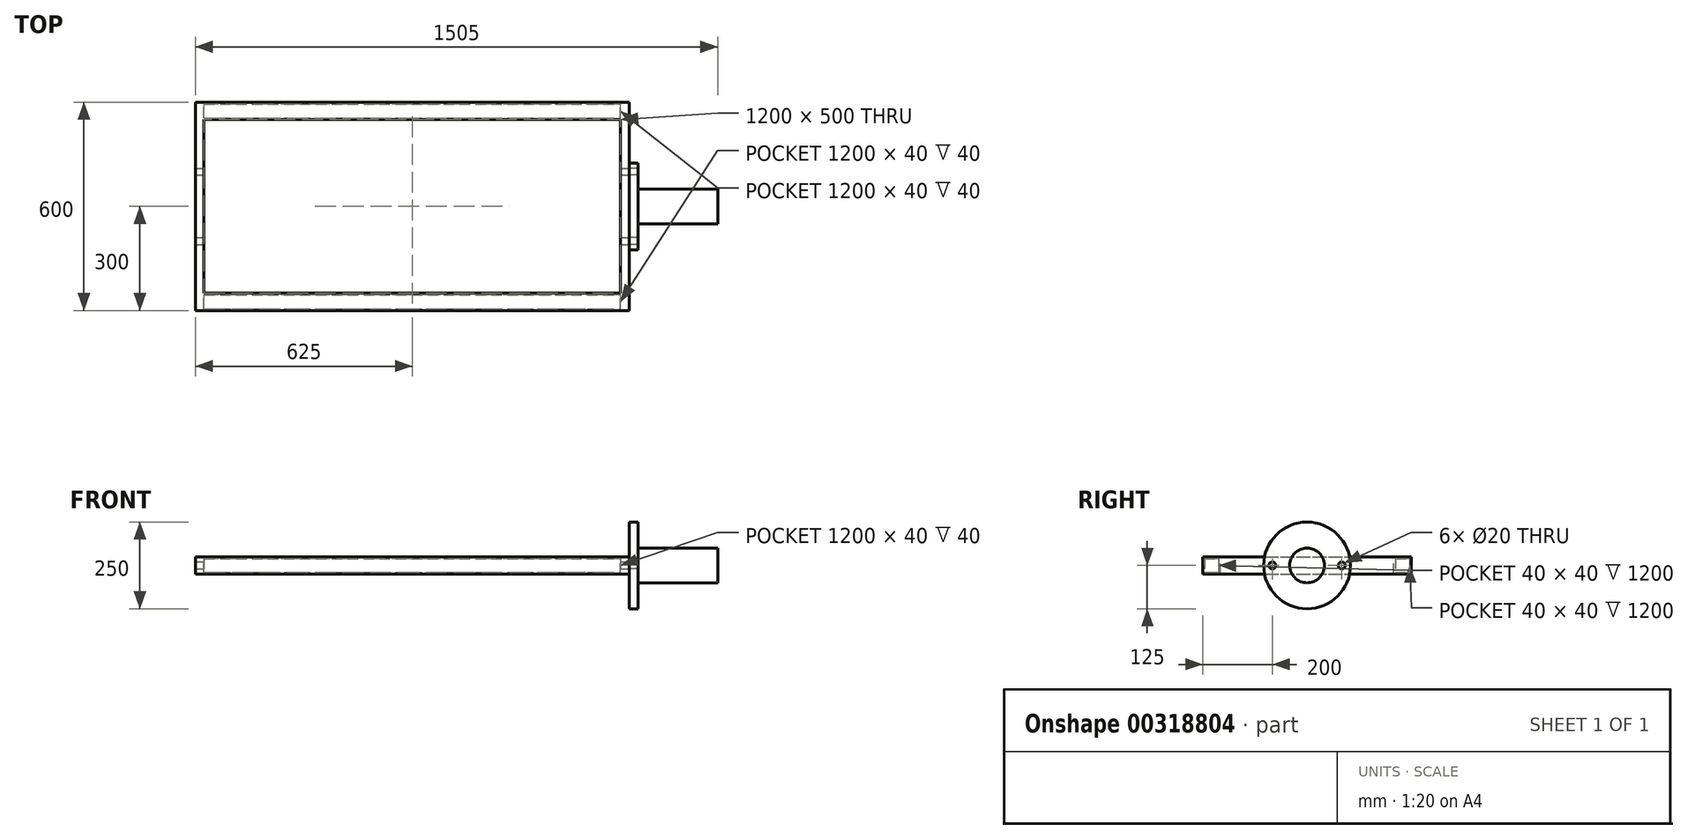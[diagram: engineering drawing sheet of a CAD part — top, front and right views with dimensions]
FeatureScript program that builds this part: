
annotation { "Feature Type Name" : "Feature", "Feature Type Description" : "" }
export const myFeature = defineFeature(function(context is Context, id is Id, definition is map)
    precondition{}
    {
        {
            var Q0;
            Q0=qCreatedBy(makeId("Right.planeOp"),FACE);
            var sketch = newSketch(context, id + "F0", { "sketchPlane" : qUnion([Q0])});
            skCircle(sketch, "E0", {"center": v(0, 0) * mm, "radius": 50 * mm});
            skSolve(sketch);
        }
        {
            var Q0;
            Q0=makeQuery(id+"F0.imprint","IMPRINT",FACE,{"disambiguationData":[TD([[makeQuery(id+"F0.imprint","IMPRINT",EDGE,{"derivedFrom":sQuery(id+"F0.wireOp",EDGE,"E0")}),1.0]])]});
            extrude(context, id + "F1", {"entities" : qUnion([Q0]), "depth" : 230 * mm});
        }
        {
            var Q0;
            Q0=makeQuery(id+"F1.opExtrude","CAP_FACE",FACE,{"disambiguationData":[OSD([sQuery(id+"F0.wireOp",EDGE,"E0")])],"isStart":true});
            var sketch = newSketch(context, id + "F2", { "sketchPlane" : qUnion([Q0])});
            skCircle(sketch, "E1", {"center": v(0, 0) * mm, "radius": 125 * mm});
            skSolve(sketch);
        }
        {
            var Q0;
            Q0=makeQuery(id+"F2.imprint","IMPRINT",FACE,{"disambiguationData":[TD([[makeQuery(id+"F2.imprint","IMPRINT",EDGE,{"derivedFrom":makeQuery(id+"F1.opExtrude","CAP_EDGE",EDGE,{"disambiguationData":[OSD([sQuery(id+"F0.wireOp",EDGE,"E0")])],"isStart":true})}),-1.0]])]});
            var Q1;
            Q1=makeQuery(id+"F2.imprint","IMPRINT",FACE,{"disambiguationData":[TD([[makeQuery(id+"F2.imprint","IMPRINT",EDGE,{"derivedFrom":sQuery(id+"F2.wireOp",EDGE,"E1")}),1.0]])]});
            extrude(context, id + "F3", {"entities" : qUnion([Q0, Q1]), "operationType" : NewBodyOperationType.ADD, "depth" : 25 * mm});
        }
        {
            var Q0;
            Q0=makeQuery(id+"F3.opExtrude","CAP_FACE",FACE,{"disambiguationData":[OSD([sQuery(id+"F2.wireOp",EDGE,"E1")])],"isStart":false});
            var sketch = newSketch(context, id + "F4", { "sketchPlane" : qUnion([Q0])});
            skLineSegment(sketch, "E2", {"start": v(0, 0) * mm, "end": v(100, 0) * mm, "construction": true});
            skCircle(sketch, "E3", {"center": v(100, 0) * mm, "radius": 10 * mm});
            skCircle(sketch, "E4.MirrorC", {"center": v(-100, 0) * mm, "radius": 10 * mm});
            skSolve(sketch);
        }
        {
            var Q0;
            Q0=qSketchRegion(id+"F4",true);
            var Q1;
            Q1=makeQuery(id+"F3.opExtrude","CAP_FACE",FACE,{"disambiguationData":[OSD([sQuery(id+"F2.wireOp",EDGE,"E1")])],"isStart":true});
            extrude(context, id + "F5", {"entities" : qUnion([Q0]), "operationType" : NewBodyOperationType.REMOVE, "endBound" : BoundingType.UP_TO_SURFACE, "oppositeDirection" : true, "endBoundEntityFace" : qUnion([Q1]), "depth" : 25 * mm});
        }
        {
            var Q0;
            Q0=makeQuery(id+"F3.opExtrude","CAP_FACE",FACE,{"disambiguationData":[OSD([sQuery(id+"F2.wireOp",EDGE,"E1")])],"isStart":false});
            var sketch = newSketch(context, id + "F6", { "sketchPlane" : qUnion([Q0])});
            skLineSegment(sketch, "E5", {"start": v(0, -25) * mm, "end": v(300, -25) * mm});
            skLineSegment(sketch, "E6", {"start": v(300, -25) * mm, "end": v(300, 0) * mm});
            skLineSegment(sketch, "E7.MirrorCS", {"start": v(0, -25) * mm, "end": v(-300, -25) * mm});
            skLineSegment(sketch, "E8.MirrorCS", {"start": v(-300, -25) * mm, "end": v(-300, 0) * mm});
            skLineSegment(sketch, "E9.MirrorCS", {"start": v(300, 25) * mm, "end": v(300, 0) * mm});
            skLineSegment(sketch, "E10.MirrorCS", {"start": v(0, 25) * mm, "end": v(300, 25) * mm});
            skLineSegment(sketch, "E11.MirrorCS", {"start": v(-300, 25) * mm, "end": v(-300, 0) * mm});
            skLineSegment(sketch, "E12.MirrorCS", {"start": v(0, 25) * mm, "end": v(-300, 25) * mm});
            skCircle(sketch, "E13.0", {"center": v(100, 0) * mm, "radius": 10 * mm});
            skCircle(sketch, "E14.0", {"center": v(-100, 0) * mm, "radius": 10 * mm});
            skSolve(sketch);
        }
        {
            var Q0;
            {var subQ4=sQuery(id+"F6.wireOp",EDGE,"E8.MirrorCS");Q0=makeQuery(id+"F6.imprint","IMPRINT",FACE,{"disambiguationData":[TD([[makeQuery(id+"F6.imprint","IMPRINT",EDGE,{"derivedFrom":subQ4}),-1.0]])]});}
            var Q1;
            Q1=makeQuery(id+"F6.imprint","IMPRINT",FACE,{"disambiguationData":[TD([[makeQuery(id+"F6.imprint","IMPRINT",EDGE,{"derivedFrom":sQuery(id+"F6.wireOp",EDGE,"E13.0")}),-1.0]])]});
            var Q2;
            {var subQ4=sQuery(id+"F6.wireOp",EDGE,"E6");Q2=makeQuery(id+"F6.imprint","IMPRINT",FACE,{"disambiguationData":[TD([[makeQuery(id+"F6.imprint","IMPRINT",EDGE,{"derivedFrom":subQ4}),1.0]])]});}
            extrude(context, id + "F7", {"entities" : qUnion([Q0, Q1, Q2]), "depth" : 25 * mm});
        }
        {
            var Q0;
            Q0=makeQuery(id+"F7.opExtrude","CAP_FACE",FACE,{"disambiguationData":[OSD([sQuery(id+"F6.wireOp",EDGE,"E5"),sQuery(id+"F6.wireOp",EDGE,"E6"),sQuery(id+"F6.wireOp",EDGE,"E7.MirrorCS"),sQuery(id+"F6.wireOp",EDGE,"E8.MirrorCS"),sQuery(id+"F6.wireOp",EDGE,"E9.MirrorCS"),sQuery(id+"F6.wireOp",EDGE,"E10.MirrorCS"),sQuery(id+"F6.wireOp",EDGE,"E11.MirrorCS"),sQuery(id+"F6.wireOp",EDGE,"E12.MirrorCS"),sQuery(id+"F6.wireOp",EDGE,"E13.0"),sQuery(id+"F6.wireOp",EDGE,"E14.0")])],"isStart":false});
            var sketch = newSketch(context, id + "F8", { "sketchPlane" : qUnion([Q0])});
            skLineSegment(sketch, "E15.bottom", {"start": v(300, -25) * mm, "end": v(250, -25) * mm});
            skLineSegment(sketch, "E15.top", {"start": v(300, 25) * mm, "end": v(250, 25) * mm});
            skLineSegment(sketch, "E15.left", {"start": v(300, -25) * mm, "end": v(300, 25) * mm});
            skLineSegment(sketch, "E15.right", {"start": v(250, -25) * mm, "end": v(250, 25) * mm});
            skLineSegment(sketch, "E16.bottom", {"start": v(-300, -25) * mm, "end": v(-250, -25) * mm});
            skLineSegment(sketch, "E16.top", {"start": v(-300, 25) * mm, "end": v(-250, 25) * mm});
            skLineSegment(sketch, "E16.left", {"start": v(-300, -25) * mm, "end": v(-300, 25) * mm});
            skLineSegment(sketch, "E16.right", {"start": v(-250, -25) * mm, "end": v(-250, 25) * mm});
            skLineSegment(sketch, "E17", {"start": v(250, -25) * mm, "end": v(300, 25) * mm, "construction": true});
            skLineSegment(sketch, "E18", {"start": v(250, 25) * mm, "end": v(300, -25) * mm, "construction": true});
            skLineSegment(sketch, "E19", {"start": v(-250, 25) * mm, "end": v(-300, -25) * mm, "construction": true});
            skLineSegment(sketch, "E20", {"start": v(-300, 25) * mm, "end": v(-250, -25) * mm, "construction": true});
            skLineSegment(sketch, "E21.bottom", {"start": v(295, 20) * mm, "end": v(255, 20) * mm});
            skLineSegment(sketch, "E21.top", {"start": v(295, -20) * mm, "end": v(255, -20) * mm});
            skLineSegment(sketch, "E21.left", {"start": v(295, 20) * mm, "end": v(295, -20) * mm});
            skLineSegment(sketch, "E21.right", {"start": v(255, 20) * mm, "end": v(255, -20) * mm});
            skPoint(sketch, "E21.middle", {"position": v(275, 0) * mm});
            skLineSegment(sketch, "E22.bottom", {"start": v(-255, 20) * mm, "end": v(-295, 20) * mm});
            skLineSegment(sketch, "E22.top", {"start": v(-255, -20) * mm, "end": v(-295, -20) * mm});
            skLineSegment(sketch, "E22.left", {"start": v(-255, 20) * mm, "end": v(-255, -20) * mm});
            skLineSegment(sketch, "E22.right", {"start": v(-295, 20) * mm, "end": v(-295, -20) * mm});
            skPoint(sketch, "E22.middle", {"position": v(-275, 0) * mm});
            skSolve(sketch);
        }
        {
            var Q0;
            Q0=qSketchRegion(id+"F8",true);
            extrude(context, id + "F9", {"entities" : qUnion([Q0]), "operationType" : NewBodyOperationType.ADD, "depth" : 1200 * mm});
        }
        {
            var Q0;
            Q0=makeQuery(id+"F9.opExtrude","CAP_FACE",FACE,{"disambiguationData":[OSD([sQuery(id+"F8.wireOp",EDGE,"E15.bottom"),sQuery(id+"F8.wireOp",EDGE,"E15.top"),sQuery(id+"F8.wireOp",EDGE,"E15.left"),sQuery(id+"F8.wireOp",EDGE,"E15.right"),sQuery(id+"F8.wireOp",EDGE,"E21.bottom"),sQuery(id+"F8.wireOp",EDGE,"E21.top"),sQuery(id+"F8.wireOp",EDGE,"E21.left"),sQuery(id+"F8.wireOp",EDGE,"E21.right")])],"isStart":false});
            var sketch = newSketch(context, id + "F10", { "sketchPlane" : qUnion([Q0])});
            skLineSegment(sketch, "E23.bottom", {"start": v(300, -25) * mm, "end": v(-300, -25) * mm});
            skLineSegment(sketch, "E23.top", {"start": v(300, 25) * mm, "end": v(-300, 25) * mm});
            skLineSegment(sketch, "E23.left", {"start": v(300, -25) * mm, "end": v(300, 25) * mm});
            skLineSegment(sketch, "E23.right", {"start": v(-300, -25) * mm, "end": v(-300, 25) * mm});
            skCircle(sketch, "E24.0", {"center": v(100, 0) * mm, "radius": 10 * mm});
            skCircle(sketch, "E25.0", {"center": v(-100, 0) * mm, "radius": 10 * mm});
            skSolve(sketch);
        }
        {
            var Q0;
            Q0=qSketchRegion(id+"F10",true);
            extrude(context, id + "F11", {"entities" : qUnion([Q0]), "operationType" : NewBodyOperationType.ADD, "depth" : 25 * mm});
        }
    });
